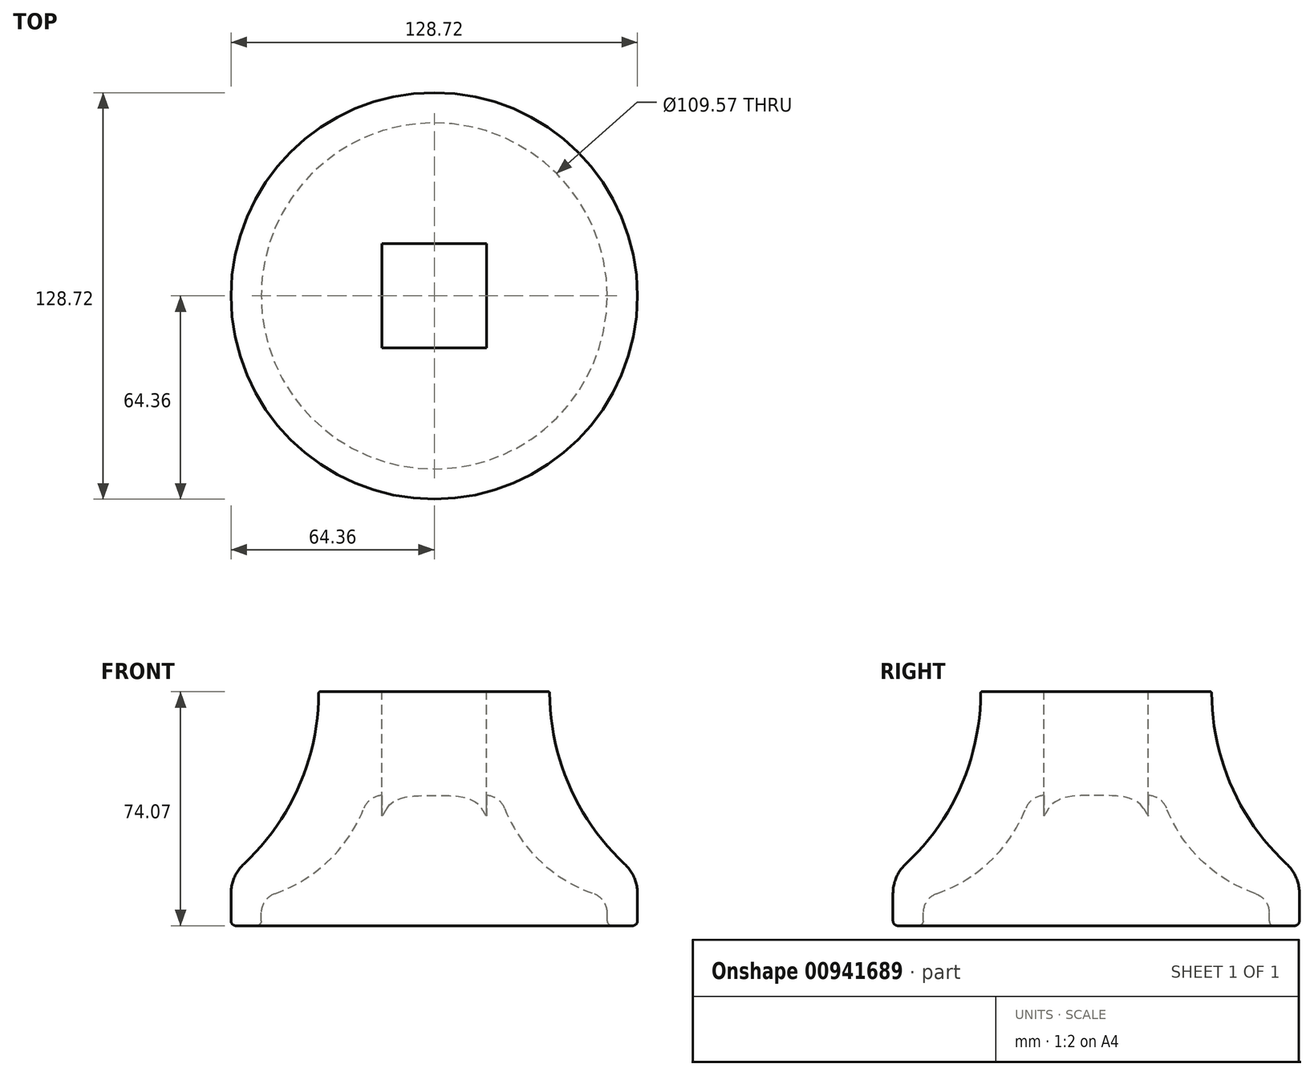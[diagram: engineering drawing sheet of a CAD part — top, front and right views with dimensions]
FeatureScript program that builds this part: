
annotation { "Feature Type Name" : "Feature", "Feature Type Description" : "" }
export const myFeature = defineFeature(function(context is Context, id is Id, definition is map)
    precondition{}
    {
        {
            var Q0;
            Q0=qCreatedBy(makeId("Front.planeOp"),FACE);
            var sketch = newSketch(context, id + "F0", { "sketchPlane" : qUnion([Q0])});
            skLineSegment(sketch, "E0", {"start": v(0, 0) * mm, "end": v(36.19, 0) * mm});
            skArc(sketch, "E1", {"start": v(36.57, -0.38) * mm, "mid": v(42.84, -29.92) * mm, "end": v(60.31, -54.55) * mm});
            skLineSegment(sketch, "E2", {"start": v(54.78, -72.55) * mm, "end": v(54.78, -69.96) * mm});
            skLineSegment(sketch, "E3", {"start": v(0, 0) * mm, "end": v(0, -32.85) * mm});
            skLineSegment(sketch, "E4", {"start": v(0, -32.85) * mm, "end": v(16.38, -32.85) * mm});
            skArc(sketch, "E5", {"start": v(22.3, -36.88) * mm, "mid": v(33.43, -53.51) * mm, "end": v(50.5, -63.96) * mm});
            skPoint(sketch, "E6.visualSharp", {"position": v(64.36, -74.07) * mm});
            skPoint(sketch, "E7.visualSharp", {"position": v(64.36, -58.06) * mm});
            skArc(sketch, "E7.filletArc", {"start": v(64.36, -63.84) * mm, "mid": v(63.3, -58.78) * mm, "end": v(60.31, -54.55) * mm});
            skPoint(sketch, "E8.visualSharp", {"position": v(36.57, 0) * mm});
            skArc(sketch, "E8.filletArc", {"start": v(36.57, -0.38) * mm, "mid": v(36.46, -0.11) * mm, "end": v(36.19, 0) * mm});
            skPoint(sketch, "E9.visualSharp", {"position": v(20.92, -32.85) * mm});
            skArc(sketch, "E9.filletArc", {"start": v(22.3, -36.88) * mm, "mid": v(19.96, -33.95) * mm, "end": v(16.38, -32.85) * mm});
            skPoint(sketch, "E10.visualSharp", {"position": v(54.78, -65.21) * mm});
            skArc(sketch, "E10.filletArc", {"start": v(54.78, -69.96) * mm, "mid": v(53.6, -66.28) * mm, "end": v(50.5, -63.96) * mm});
            skPoint(sketch, "E11.visualSharp", {"position": v(54.78, -74.07) * mm});
            skArc(sketch, "E11.filletArc", {"start": v(54.78, -72.55) * mm, "mid": v(55.23, -73.63) * mm, "end": v(56.3, -74.07) * mm});
            skLineSegment(sketch, "E12", {"start": v(56.3, -74.07) * mm, "end": v(62.83, -74.07) * mm});
            skLineSegment(sketch, "E13", {"start": v(64.36, -63.84) * mm, "end": v(64.36, -72.55) * mm});
            skArc(sketch, "E14.filletArc", {"start": v(62.83, -74.07) * mm, "mid": v(63.91, -73.63) * mm, "end": v(64.36, -72.55) * mm});
            skSolve(sketch);
        }
        {
            var Q0;
            Q0=makeQuery(id+"F0.imprint","IMPRINT",FACE,{"disambiguationData":[TD([[makeQuery(id+"F0.imprint","IMPRINT",EDGE,{"derivedFrom":sQuery(id+"F0.wireOp",EDGE,"E0")}),-1.0]])]});
            var Q1;
            Q1=sQuery(id+"F0.wireOp",EDGE,"E3");
            revolve(context, id + "F1", {"surfaceOperationType" : NewSurfaceOperationType.NEW, "entities" : qUnion([Q0]), "axis" : qUnion([Q1]), "revolveType" : RevolveType.FULL});
        }
        {
            var Q0;
            Q0=makeQuery(id+"F1.opRevolve","SWEPT_FACE",FACE,{"disambiguationData":[OSD([sQuery(id+"F0.wireOp",EDGE,"E0")])]});
            var sketch = newSketch(context, id + "F2", { "sketchPlane" : qUnion([Q0])});
            skSolve(sketch);
        }
        {
            var Q0;
            Q0=makeQuery(id+"F2.imprint","IMPRINT",FACE,{"disambiguationData":[TD([[makeQuery(id+"F2.imprint","IMPRINT",EDGE,{"derivedFrom":makeQuery(id+"F1.opRevolve","SWEPT_EDGE",EDGE,{"disambiguationData":[OSD([sQuery(id+"F0.wireOp",EDGE,"E0"),sQuery(id+"F0.wireOp",EDGE,"E8.filletArc")])]})}),1.0]])]});
            var sketch = newSketch(context, id + "F3", { "sketchPlane" : qUnion([Q0])});
            skLineSegment(sketch, "E15.bottom", {"start": v(16.51, -16.51) * mm, "end": v(-16.51, -16.51) * mm});
            skLineSegment(sketch, "E15.top", {"start": v(16.51, 16.51) * mm, "end": v(-16.51, 16.51) * mm});
            skLineSegment(sketch, "E15.left", {"start": v(16.51, -16.51) * mm, "end": v(16.51, 16.51) * mm});
            skLineSegment(sketch, "E15.right", {"start": v(-16.51, -16.51) * mm, "end": v(-16.51, 16.51) * mm});
            skPoint(sketch, "E15.middle", {"position": v(0, 0) * mm});
            skSolve(sketch);
        }
        {
            var Q0;
            Q0=makeQuery(id+"F3.imprint","IMPRINT",FACE,{"disambiguationData":[TD([[makeQuery(id+"F3.imprint","IMPRINT",EDGE,{"derivedFrom":sQuery(id+"F3.wireOp",EDGE,"E15.bottom")}),-1.0]])]});
            extrude(context, id + "F4", {"entities" : qUnion([Q0]), "operationType" : NewBodyOperationType.REMOVE, "endBound" : BoundingType.THROUGH_ALL, "oppositeDirection" : true, "depth" : 25.4 * mm, "offsetDistance" : 25.4 * mm});
        }
    });
